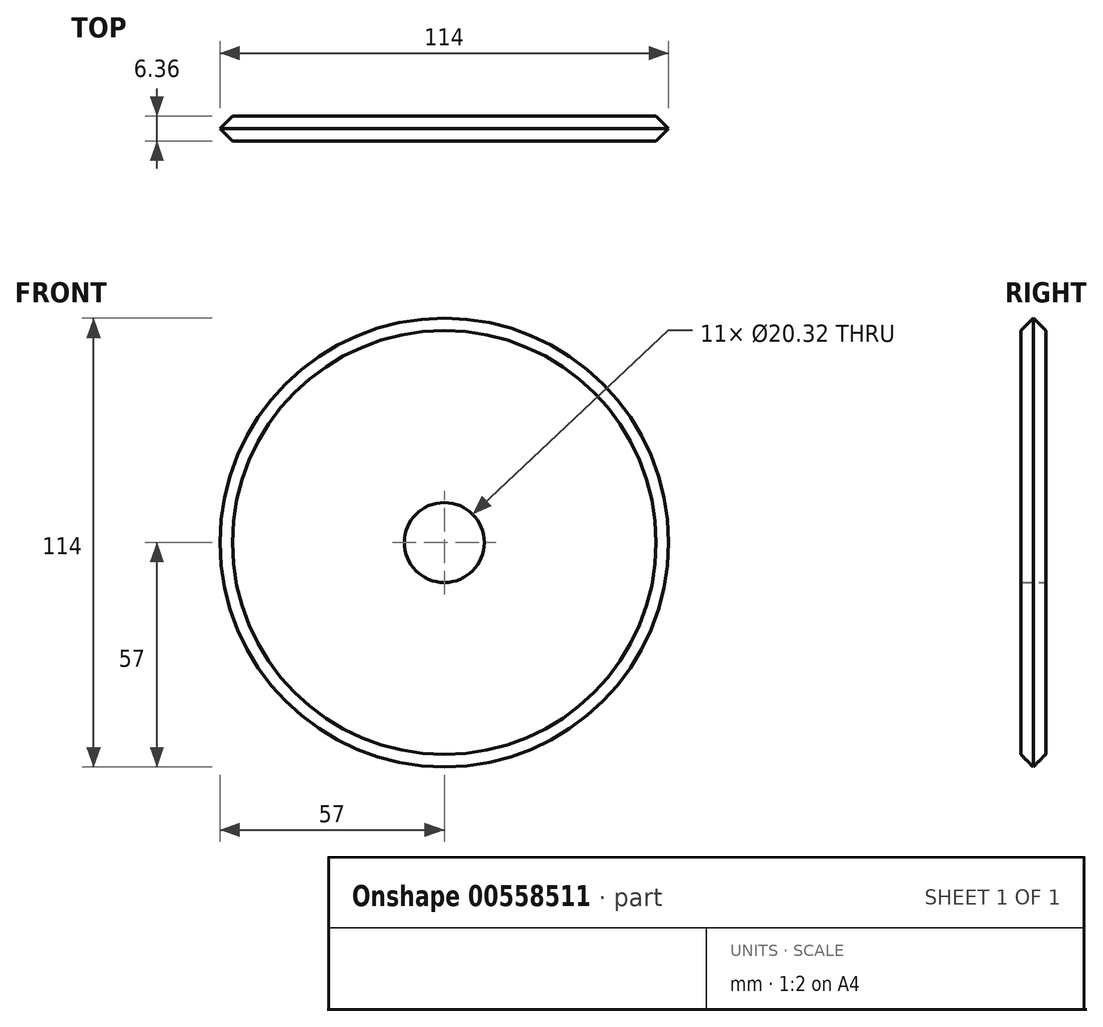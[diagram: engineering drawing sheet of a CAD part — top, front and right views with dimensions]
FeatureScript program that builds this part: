
annotation { "Feature Type Name" : "Feature", "Feature Type Description" : "" }
export const myFeature = defineFeature(function(context is Context, id is Id, definition is map)
    precondition{}
    {
        {
            var Q0;
            Q0=qCreatedBy(makeId("Front.planeOp"),FACE);
            var sketch = newSketch(context, id + "F0", { "sketchPlane" : qUnion([Q0])});
            skCircle(sketch, "E0", {"center": v(0, 0) * mm, "radius": 57 * mm});
            skCircle(sketch, "E1", {"center": v(0, 0) * mm, "radius": 10.16 * mm});
            skSolve(sketch);
        }
        {
            var Q0;
            Q0=makeQuery(id+"F0.imprint","IMPRINT",FACE,{"disambiguationData":[TD([[makeQuery(id+"F0.imprint","IMPRINT",EDGE,{"derivedFrom":sQuery(id+"F0.wireOp",EDGE,"E0")}),1.0]])]});
            extrude(context, id + "F1", {"entities" : qUnion([Q0]), "endBound" : BoundingType.SYMMETRIC, "depth" : 6.35 * mm, "offsetDistance" : 25.4 * mm});
        }
        {
            var Q0;
            Q0=makeQuery(id+"F1.opExtrude","CAP_EDGE",EDGE,{"disambiguationData":[OSD([sQuery(id+"F0.wireOp",EDGE,"E0")])],"isStart":true});
            chamfer(context, id + "F2", {"entities" : qUnion([Q0]), "width" : 3.17 * mm, "tangentPropagation" : true});
        }
        {
            var Q0;
            Q0=makeQuery(id+"F1.opExtrude","CAP_EDGE",EDGE,{"disambiguationData":[OSD([sQuery(id+"F0.wireOp",EDGE,"E0")])],"isStart":false});
            chamfer(context, id + "F3", {"entities" : qUnion([Q0]), "width" : 3.17 * mm, "tangentPropagation" : true});
        }
    });
